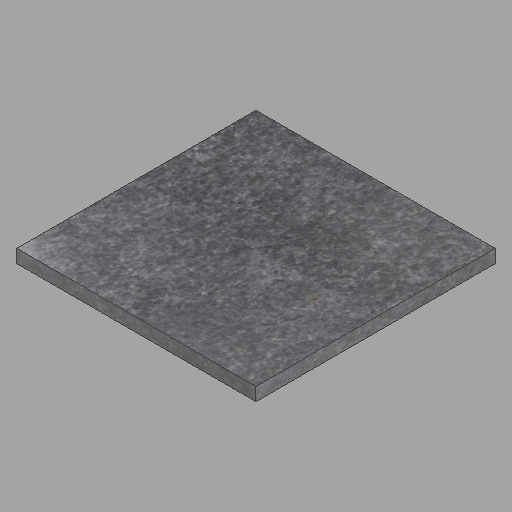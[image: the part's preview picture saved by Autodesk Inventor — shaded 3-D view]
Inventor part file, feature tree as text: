
AUTODESK INVENTOR PART (.ipt)
format: ipt  version: 2023 (Build 270158030, 158C)  size: 237,568 bytes
history: native  units: in
note: dims shown in document units (in); Inventor stores cm internally (conversion verified against a paired STEP export)
features: extrude x1, sketch x1
ambient origin geometry x8: Origin, YZ Plane, XZ Plane, XY Plane, X Axis, Y Axis, Z Axis, Center Point
bodies: Solid1 (feature_tree)
feature tree (2):
  extrude  "Extrusion1"  Depth=36.0in
  sketch  "Sketch1"  dims[d0=36.0in d1=36.0in d2=2.0in d3=0.0in]
